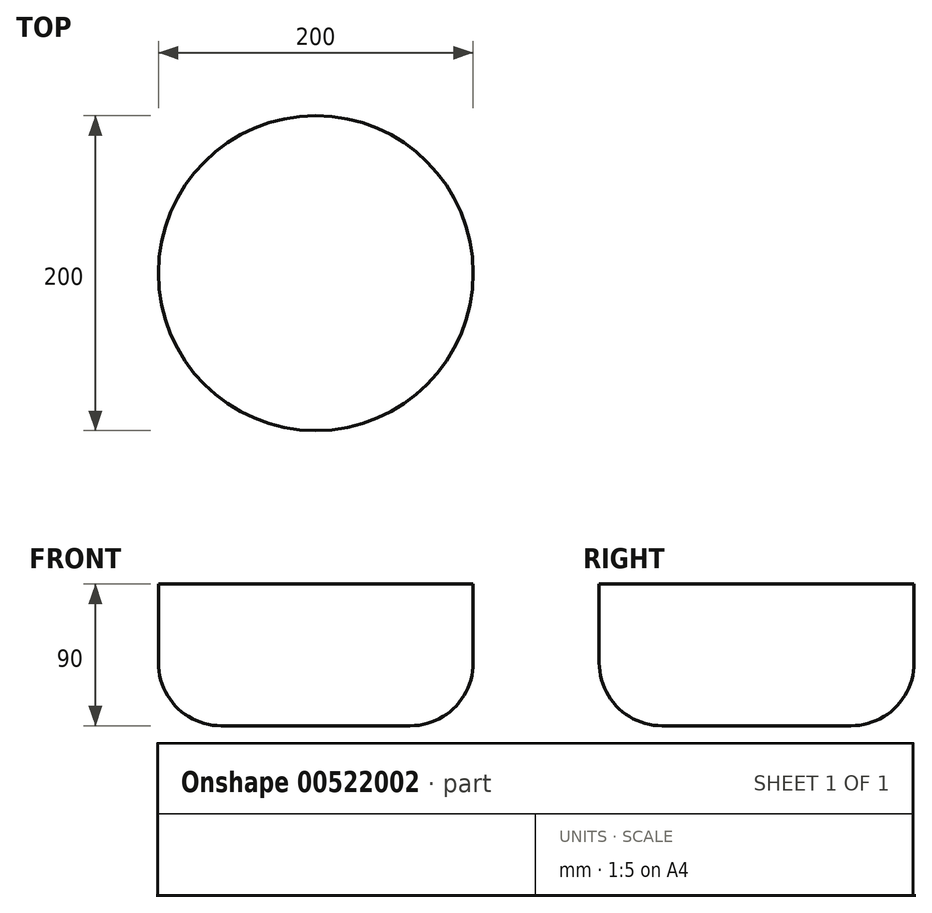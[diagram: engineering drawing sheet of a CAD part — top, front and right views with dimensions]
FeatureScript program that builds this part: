
annotation { "Feature Type Name" : "Feature", "Feature Type Description" : "" }
export const myFeature = defineFeature(function(context is Context, id is Id, definition is map)
    precondition{}
    {
        {
            var Q0;
            Q0=qCreatedBy(makeId("Top.planeOp"),FACE);
            var sketch = newSketch(context, id + "F0", { "sketchPlane" : qUnion([Q0])});
            skCircle(sketch, "E0", {"center": v(0, 0) * mm, "radius": 100 * mm});
            skSolve(sketch);
        }
        {
            var Q0;
            Q0=makeQuery(id+"F0.imprint","IMPRINT",FACE,{"disambiguationData":[TD([[makeQuery(id+"F0.imprint","IMPRINT",EDGE,{"derivedFrom":sQuery(id+"F0.wireOp",EDGE,"E0")}),1.0]])]});
            extrude(context, id + "F1", {"entities" : qUnion([Q0]), "depth" : 90 * mm, "offsetDistance" : 25 * mm});
        }
        {
            var Q0;
            Q0=makeQuery(id+"F1.opExtrude","CAP_EDGE",EDGE,{"disambiguationData":[OSD([sQuery(id+"F0.wireOp",EDGE,"E0")])],"isStart":true});
            fillet(context, id + "F2", {"entities" : qUnion([Q0]), "radius" : 40 * mm, "tangentPropagation" : true, "allowEdgeOverflow" : false});
        }
    });
